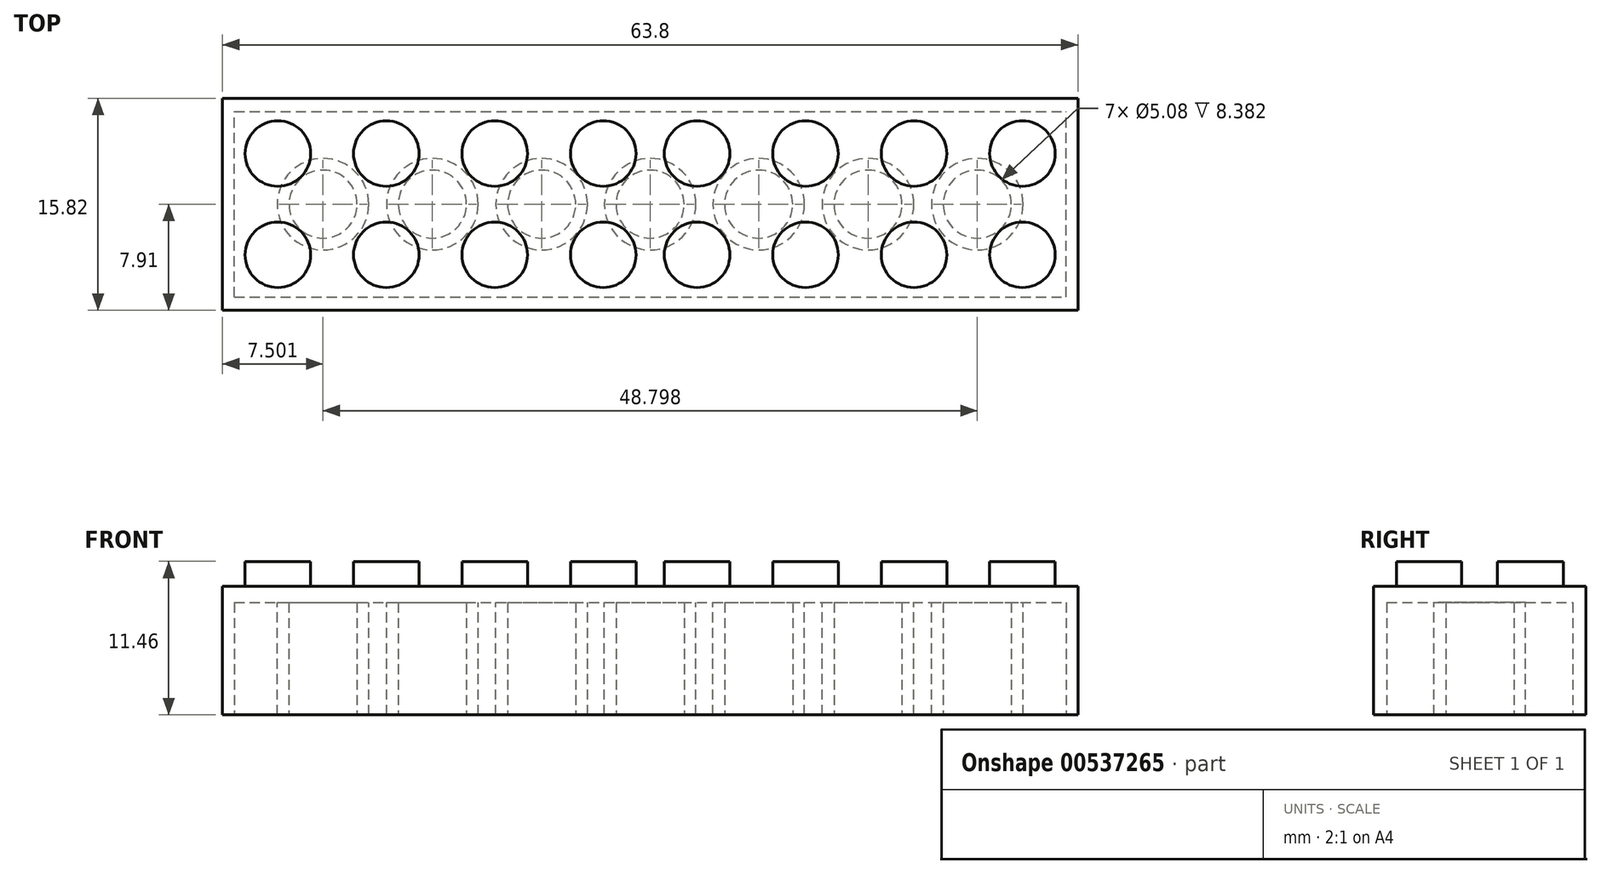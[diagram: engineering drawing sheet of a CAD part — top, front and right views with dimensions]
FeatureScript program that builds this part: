
annotation { "Feature Type Name" : "Feature", "Feature Type Description" : "" }
export const myFeature = defineFeature(function(context is Context, id is Id, definition is map)
    precondition{}
    {
        {
            var Q0;
            Q0=qCreatedBy(makeId("Top.planeOp"),FACE);
            var sketch = newSketch(context, id + "F0", { "sketchPlane" : qUnion([Q0])});
            skLineSegment(sketch, "E0.bottom", {"start": v(31.9, -7.91) * mm, "end": v(-31.9, -7.91) * mm});
            skLineSegment(sketch, "E0.top", {"start": v(31.9, 7.91) * mm, "end": v(-31.9, 7.91) * mm});
            skLineSegment(sketch, "E0.left", {"start": v(31.9, -7.91) * mm, "end": v(31.9, 7.91) * mm});
            skLineSegment(sketch, "E0.right", {"start": v(-31.9, -7.91) * mm, "end": v(-31.9, 7.91) * mm});
            skPoint(sketch, "E0.middle", {"position": v(0, 0) * mm});
            skSolve(sketch);
        }
        {
            var Q0;
            Q0=makeQuery(id+"F0.imprint","IMPRINT",FACE,{"disambiguationData":[TD([[makeQuery(id+"F0.imprint","IMPRINT",EDGE,{"derivedFrom":sQuery(id+"F0.wireOp",EDGE,"E0.bottom")}),-1.0]])]});
            extrude(context, id + "F1", {"entities" : qUnion([Q0]), "depth" : 9.6 * mm, "offsetDistance" : 25.4 * mm});
        }
        {
            var Q0;
            Q0=makeQuery(id+"F1.opExtrude","CAP_FACE",FACE,{"disambiguationData":[OSD([sQuery(id+"F0.wireOp",EDGE,"E0.bottom"),sQuery(id+"F0.wireOp",EDGE,"E0.top"),sQuery(id+"F0.wireOp",EDGE,"E0.left"),sQuery(id+"F0.wireOp",EDGE,"E0.right")])],"isStart":false});
            var sketch = newSketch(context, id + "F2", { "sketchPlane" : qUnion([Q0])});
            skCircle(sketch, "E1", {"center": v(-27.77, 3.78) * mm, "radius": 2.44 * mm});
            skCircle(sketch, "E2", {"center": v(-19.68, 3.78) * mm, "radius": 2.44 * mm});
            skCircle(sketch, "E3", {"center": v(-11.59, 3.78) * mm, "radius": 2.44 * mm});
            skCircle(sketch, "E4", {"center": v(-3.5, 3.78) * mm, "radius": 2.44 * mm});
            skCircle(sketch, "E5", {"center": v(3.5, 3.78) * mm, "radius": 2.44 * mm});
            skCircle(sketch, "E6", {"center": v(11.59, 3.78) * mm, "radius": 2.44 * mm});
            skCircle(sketch, "E7", {"center": v(19.68, 3.78) * mm, "radius": 2.44 * mm});
            skCircle(sketch, "E8", {"center": v(27.77, 3.78) * mm, "radius": 2.44 * mm});
            skCircle(sketch, "E9", {"center": v(27.77, -3.78) * mm, "radius": 2.44 * mm});
            skCircle(sketch, "E10", {"center": v(19.68, -3.78) * mm, "radius": 2.44 * mm});
            skCircle(sketch, "E11", {"center": v(11.59, -3.78) * mm, "radius": 2.44 * mm});
            skCircle(sketch, "E12", {"center": v(3.5, -3.78) * mm, "radius": 2.44 * mm});
            skCircle(sketch, "E13", {"center": v(-3.5, -3.78) * mm, "radius": 2.44 * mm});
            skCircle(sketch, "E14", {"center": v(-11.59, -3.78) * mm, "radius": 2.44 * mm});
            skCircle(sketch, "E15", {"center": v(-19.68, -3.78) * mm, "radius": 2.44 * mm});
            skCircle(sketch, "E16", {"center": v(-27.77, -3.78) * mm, "radius": 2.44 * mm});
            skSolve(sketch);
        }
        {
            var Q0;
            Q0=makeQuery(id+"F2.imprint","IMPRINT",FACE,{"disambiguationData":[TD([[makeQuery(id+"F2.imprint","IMPRINT",EDGE,{"derivedFrom":sQuery(id+"F2.wireOp",EDGE,"E1")}),1.0]])]});
            var Q1;
            Q1=makeQuery(id+"F2.imprint","IMPRINT",FACE,{"disambiguationData":[TD([[makeQuery(id+"F2.imprint","IMPRINT",EDGE,{"derivedFrom":sQuery(id+"F2.wireOp",EDGE,"E11")}),1.0]])]});
            var Q2;
            Q2=makeQuery(id+"F2.imprint","IMPRINT",FACE,{"disambiguationData":[TD([[makeQuery(id+"F2.imprint","IMPRINT",EDGE,{"derivedFrom":sQuery(id+"F2.wireOp",EDGE,"E13")}),1.0]])]});
            var Q3;
            Q3=makeQuery(id+"F2.imprint","IMPRINT",FACE,{"disambiguationData":[TD([[makeQuery(id+"F2.imprint","IMPRINT",EDGE,{"derivedFrom":sQuery(id+"F2.wireOp",EDGE,"E12")}),1.0]])]});
            var Q4;
            Q4=makeQuery(id+"F2.imprint","IMPRINT",FACE,{"disambiguationData":[TD([[makeQuery(id+"F2.imprint","IMPRINT",EDGE,{"derivedFrom":sQuery(id+"F2.wireOp",EDGE,"E10")}),1.0]])]});
            var Q5;
            Q5=makeQuery(id+"F2.imprint","IMPRINT",FACE,{"disambiguationData":[TD([[makeQuery(id+"F2.imprint","IMPRINT",EDGE,{"derivedFrom":sQuery(id+"F2.wireOp",EDGE,"E9")}),1.0]])]});
            var Q6;
            Q6=makeQuery(id+"F2.imprint","IMPRINT",FACE,{"disambiguationData":[TD([[makeQuery(id+"F2.imprint","IMPRINT",EDGE,{"derivedFrom":sQuery(id+"F2.wireOp",EDGE,"E8")}),1.0]])]});
            var Q7;
            Q7=makeQuery(id+"F2.imprint","IMPRINT",FACE,{"disambiguationData":[TD([[makeQuery(id+"F2.imprint","IMPRINT",EDGE,{"derivedFrom":sQuery(id+"F2.wireOp",EDGE,"E7")}),1.0]])]});
            var Q8;
            Q8=makeQuery(id+"F2.imprint","IMPRINT",FACE,{"disambiguationData":[TD([[makeQuery(id+"F2.imprint","IMPRINT",EDGE,{"derivedFrom":sQuery(id+"F2.wireOp",EDGE,"E6")}),1.0]])]});
            var Q9;
            Q9=makeQuery(id+"F2.imprint","IMPRINT",FACE,{"disambiguationData":[TD([[makeQuery(id+"F2.imprint","IMPRINT",EDGE,{"derivedFrom":sQuery(id+"F2.wireOp",EDGE,"E16")}),1.0]])]});
            var Q10;
            Q10=makeQuery(id+"F2.imprint","IMPRINT",FACE,{"disambiguationData":[TD([[makeQuery(id+"F2.imprint","IMPRINT",EDGE,{"derivedFrom":sQuery(id+"F2.wireOp",EDGE,"E5")}),1.0]])]});
            var Q11;
            Q11=makeQuery(id+"F2.imprint","IMPRINT",FACE,{"disambiguationData":[TD([[makeQuery(id+"F2.imprint","IMPRINT",EDGE,{"derivedFrom":sQuery(id+"F2.wireOp",EDGE,"E4")}),1.0]])]});
            var Q12;
            Q12=makeQuery(id+"F2.imprint","IMPRINT",FACE,{"disambiguationData":[TD([[makeQuery(id+"F2.imprint","IMPRINT",EDGE,{"derivedFrom":sQuery(id+"F2.wireOp",EDGE,"E3")}),1.0]])]});
            var Q13;
            Q13=makeQuery(id+"F2.imprint","IMPRINT",FACE,{"disambiguationData":[TD([[makeQuery(id+"F2.imprint","IMPRINT",EDGE,{"derivedFrom":sQuery(id+"F2.wireOp",EDGE,"E14")}),1.0]])]});
            var Q14;
            Q14=makeQuery(id+"F2.imprint","IMPRINT",FACE,{"disambiguationData":[TD([[makeQuery(id+"F2.imprint","IMPRINT",EDGE,{"derivedFrom":sQuery(id+"F2.wireOp",EDGE,"E15")}),1.0]])]});
            var Q15;
            Q15=makeQuery(id+"F2.imprint","IMPRINT",FACE,{"disambiguationData":[TD([[makeQuery(id+"F2.imprint","IMPRINT",EDGE,{"derivedFrom":sQuery(id+"F2.wireOp",EDGE,"E2")}),1.0]])]});
            extrude(context, id + "F3", {"entities" : qUnion([Q0, Q1, Q2, Q3, Q4, Q5, Q6, Q7, Q8, Q9, Q10, Q11, Q12, Q13, Q14, Q15]), "operationType" : NewBodyOperationType.ADD, "depth" : 1.84 * mm, "offsetDistance" : 25.4 * mm});
        }
        {
            var Q0;
            Q0=makeQuery(id+"F1.opExtrude","CAP_FACE",FACE,{"disambiguationData":[OSD([sQuery(id+"F0.wireOp",EDGE,"E0.bottom"),sQuery(id+"F0.wireOp",EDGE,"E0.top"),sQuery(id+"F0.wireOp",EDGE,"E0.left"),sQuery(id+"F0.wireOp",EDGE,"E0.right")])],"isStart":true});
            var sketch = newSketch(context, id + "F4", { "sketchPlane" : qUnion([Q0])});
            skLineSegment(sketch, "E17.bottom", {"start": v(-31.02, 6.93) * mm, "end": v(31.02, 6.93) * mm});
            skLineSegment(sketch, "E17.top", {"start": v(-31.02, -6.93) * mm, "end": v(31.02, -6.93) * mm});
            skLineSegment(sketch, "E17.left", {"start": v(-31.02, 6.93) * mm, "end": v(-31.02, -6.93) * mm});
            skLineSegment(sketch, "E17.right", {"start": v(31.02, 6.93) * mm, "end": v(31.02, -6.93) * mm});
            skPoint(sketch, "E17.middle", {"position": v(0, 0) * mm});
            skSolve(sketch);
        }
        {
            var Q0;
            Q0=makeQuery(id+"F4.imprint","IMPRINT",FACE,{"disambiguationData":[TD([[makeQuery(id+"F4.imprint","IMPRINT",EDGE,{"derivedFrom":sQuery(id+"F4.wireOp",EDGE,"E17.bottom")}),-1.0]])]});
            extrude(context, id + "F5", {"entities" : qUnion([Q0]), "operationType" : NewBodyOperationType.REMOVE, "oppositeDirection" : true, "depth" : 8.38 * mm, "offsetDistance" : 25.4 * mm});
        }
        {
            var Q0;
            Q0=makeQuery(id+"F5.boolean.opBoolean","COPY",FACE,{"derivedFrom":makeQuery(id+"F5.opExtrude","CAP_FACE",FACE,{"disambiguationData":[OSD([sQuery(id+"F4.wireOp",EDGE,"E17.bottom"),sQuery(id+"F4.wireOp",EDGE,"E17.top"),sQuery(id+"F4.wireOp",EDGE,"E17.left"),sQuery(id+"F4.wireOp",EDGE,"E17.right")])],"isStart":false})});
            var sketch = newSketch(context, id + "F6", { "sketchPlane" : qUnion([Q0])});
            skCircle(sketch, "E18", {"center": v(0, 0) * mm, "radius": 3.42 * mm});
            skCircle(sketch, "E19", {"center": v(-8.1, 0) * mm, "radius": 3.42 * mm});
            skCircle(sketch, "E20", {"center": v(-16.25, 0) * mm, "radius": 3.42 * mm});
            skCircle(sketch, "E21", {"center": v(-24.4, 0) * mm, "radius": 3.42 * mm});
            skCircle(sketch, "E22", {"center": v(8.1, 0) * mm, "radius": 3.42 * mm});
            skCircle(sketch, "E23", {"center": v(16.25, 0) * mm, "radius": 3.42 * mm});
            skCircle(sketch, "E24", {"center": v(24.4, 0) * mm, "radius": 3.42 * mm});
            skSolve(sketch);
        }
        {
            var Q0;
            Q0=makeQuery(id+"F6.imprint","IMPRINT",FACE,{"disambiguationData":[TD([[makeQuery(id+"F6.imprint","IMPRINT",EDGE,{"derivedFrom":sQuery(id+"F6.wireOp",EDGE,"E20")}),1.0]])]});
            var Q1;
            Q1=makeQuery(id+"F6.imprint","IMPRINT",FACE,{"disambiguationData":[TD([[makeQuery(id+"F6.imprint","IMPRINT",EDGE,{"derivedFrom":sQuery(id+"F6.wireOp",EDGE,"E21")}),1.0]])]});
            var Q2;
            Q2=makeQuery(id+"F6.imprint","IMPRINT",FACE,{"disambiguationData":[TD([[makeQuery(id+"F6.imprint","IMPRINT",EDGE,{"derivedFrom":sQuery(id+"F6.wireOp",EDGE,"E18")}),1.0]])]});
            var Q3;
            Q3=makeQuery(id+"F6.imprint","IMPRINT",FACE,{"disambiguationData":[TD([[makeQuery(id+"F6.imprint","IMPRINT",EDGE,{"derivedFrom":sQuery(id+"F6.wireOp",EDGE,"E19")}),1.0]])]});
            var Q4;
            Q4=makeQuery(id+"F6.imprint","IMPRINT",FACE,{"disambiguationData":[TD([[makeQuery(id+"F6.imprint","IMPRINT",EDGE,{"derivedFrom":sQuery(id+"F6.wireOp",EDGE,"E22")}),1.0]])]});
            var Q5;
            Q5=makeQuery(id+"F6.imprint","IMPRINT",FACE,{"disambiguationData":[TD([[makeQuery(id+"F6.imprint","IMPRINT",EDGE,{"derivedFrom":sQuery(id+"F6.wireOp",EDGE,"E24")}),1.0]])]});
            var Q6;
            Q6=makeQuery(id+"F6.imprint","IMPRINT",FACE,{"disambiguationData":[TD([[makeQuery(id+"F6.imprint","IMPRINT",EDGE,{"derivedFrom":sQuery(id+"F6.wireOp",EDGE,"E23")}),1.0]])]});
            extrude(context, id + "F7", {"entities" : qUnion([Q0, Q1, Q2, Q3, Q4, Q5, Q6]), "operationType" : NewBodyOperationType.ADD, "depth" : 8.38 * mm, "offsetDistance" : 25.4 * mm});
        }
        {
            var Q0;
            Q0=makeQuery(id+"F7.opExtrude","CAP_FACE",FACE,{"disambiguationData":[OSD([sQuery(id+"F6.wireOp",EDGE,"E18")])],"isStart":false});
            var sketch = newSketch(context, id + "F8", { "sketchPlane" : qUnion([Q0])});
            skCircle(sketch, "E25", {"center": v(0, 0) * mm, "radius": 2.54 * mm});
            skCircle(sketch, "E26", {"center": v(-8.1, 0) * mm, "radius": 2.54 * mm});
            skCircle(sketch, "E27", {"center": v(-16.25, 0) * mm, "radius": 2.54 * mm});
            skCircle(sketch, "E28", {"center": v(-24.4, 0) * mm, "radius": 2.54 * mm});
            skCircle(sketch, "E29", {"center": v(8.1, 0) * mm, "radius": 2.54 * mm});
            skCircle(sketch, "E30", {"center": v(16.25, 0) * mm, "radius": 2.54 * mm});
            skCircle(sketch, "E31", {"center": v(24.4, 0) * mm, "radius": 2.54 * mm});
            skSolve(sketch);
        }
        {
            var Q0;
            Q0=makeQuery(id+"F8.imprint","IMPRINT",FACE,{"disambiguationData":[TD([[makeQuery(id+"F8.imprint","IMPRINT",EDGE,{"derivedFrom":sQuery(id+"F8.wireOp",EDGE,"E28")}),1.0]])]});
            var Q1;
            Q1=makeQuery(id+"F8.imprint","IMPRINT",FACE,{"disambiguationData":[TD([[makeQuery(id+"F8.imprint","IMPRINT",EDGE,{"derivedFrom":sQuery(id+"F8.wireOp",EDGE,"E27")}),1.0]])]});
            var Q2;
            Q2=makeQuery(id+"F8.imprint","IMPRINT",FACE,{"disambiguationData":[TD([[makeQuery(id+"F8.imprint","IMPRINT",EDGE,{"derivedFrom":sQuery(id+"F8.wireOp",EDGE,"E26")}),1.0]])]});
            var Q3;
            Q3=makeQuery(id+"F8.imprint","IMPRINT",FACE,{"disambiguationData":[TD([[makeQuery(id+"F8.imprint","IMPRINT",EDGE,{"derivedFrom":sQuery(id+"F8.wireOp",EDGE,"E25")}),1.0]])]});
            var Q4;
            Q4=makeQuery(id+"F8.imprint","IMPRINT",FACE,{"disambiguationData":[TD([[makeQuery(id+"F8.imprint","IMPRINT",EDGE,{"derivedFrom":sQuery(id+"F8.wireOp",EDGE,"E29")}),1.0]])]});
            var Q5;
            Q5=makeQuery(id+"F8.imprint","IMPRINT",FACE,{"disambiguationData":[TD([[makeQuery(id+"F8.imprint","IMPRINT",EDGE,{"derivedFrom":sQuery(id+"F8.wireOp",EDGE,"E30")}),1.0]])]});
            var Q6;
            Q6=makeQuery(id+"F8.imprint","IMPRINT",FACE,{"disambiguationData":[TD([[makeQuery(id+"F8.imprint","IMPRINT",EDGE,{"derivedFrom":sQuery(id+"F8.wireOp",EDGE,"E31")}),1.0]])]});
            extrude(context, id + "F9", {"entities" : qUnion([Q0, Q1, Q2, Q3, Q4, Q5, Q6]), "operationType" : NewBodyOperationType.REMOVE, "oppositeDirection" : true, "depth" : 8.38 * mm, "offsetDistance" : 25.4 * mm});
        }
    });
